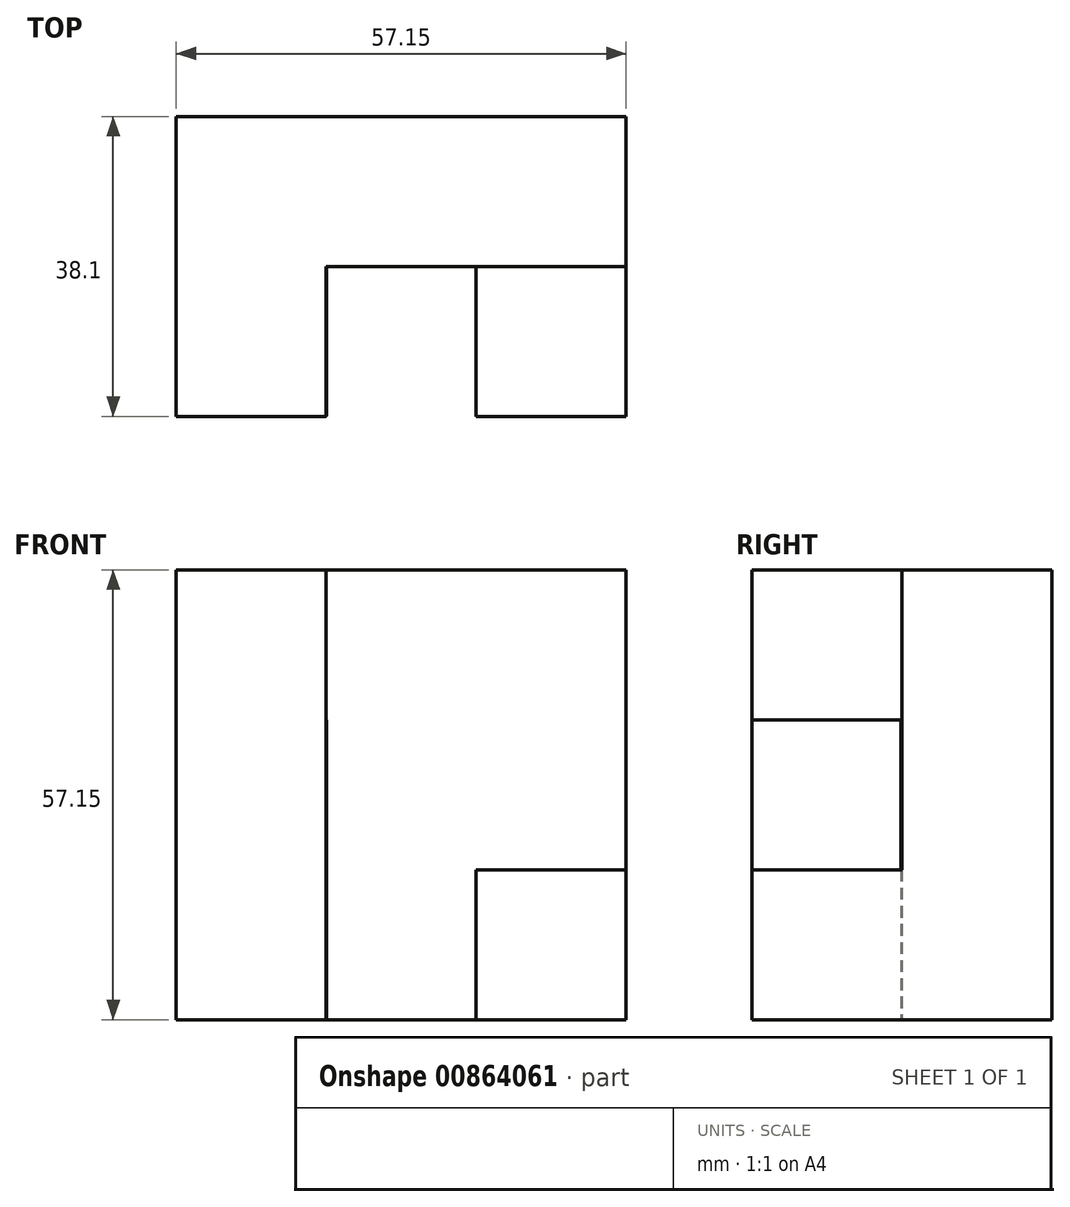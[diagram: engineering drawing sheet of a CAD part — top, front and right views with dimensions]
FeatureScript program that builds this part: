
annotation { "Feature Type Name" : "Feature", "Feature Type Description" : "" }
export const myFeature = defineFeature(function(context is Context, id is Id, definition is map)
    precondition{}
    {
        {
            var Q0;
            Q0=qCreatedBy(makeId("Front.planeOp"),FACE);
            var sketch = newSketch(context, id + "F0", { "sketchPlane" : qUnion([Q0])});
            skLineSegment(sketch, "E0", {"start": v(0, 0) * mm, "end": v(57.15, 0) * mm});
            skLineSegment(sketch, "E1", {"start": v(57.15, 0) * mm, "end": v(57.15, 19.05) * mm});
            skLineSegment(sketch, "E2", {"start": v(57.15, 19.05) * mm, "end": v(0, 19.05) * mm});
            skLineSegment(sketch, "E3", {"start": v(0, 19.05) * mm, "end": v(0, 0) * mm});
            skSolve(sketch);
        }
        {
            var Q0;
            Q0 = qSketchRegion(id + "F0", true);
            extrude(context, id + "F1", {"entities" : qUnion([Q0]), "depth" : 19.05 * mm, "offsetDistance" : 25.4 * mm});
        }
        {
            var Q0;
            Q0=makeQuery(id+"F1.opExtrude","CAP_FACE",FACE,{"disambiguationData":[OSD([sQuery(id+"F0.wireOp",EDGE,"E0"),sQuery(id+"F0.wireOp",EDGE,"E1"),sQuery(id+"F0.wireOp",EDGE,"E2"),sQuery(id+"F0.wireOp",EDGE,"E3")])],"isStart":false});
            var sketch = newSketch(context, id + "F2", { "sketchPlane" : qUnion([Q0])});
            skLineSegment(sketch, "E4.0.0", {"start": v(57.15, 19.05) * mm, "end": v(0, 19.05) * mm});
            skLineSegment(sketch, "E4.0.1", {"start": v(0, 19.05) * mm, "end": v(0, 0) * mm});
            skLineSegment(sketch, "E4.0.2", {"start": v(0, 0) * mm, "end": v(57.15, 0) * mm});
            skLineSegment(sketch, "E4.0.3", {"start": v(57.15, 0) * mm, "end": v(57.15, 19.05) * mm});
            skLineSegment(sketch, "E5", {"start": v(38.1, 19.05) * mm, "end": v(38.1, 0) * mm});
            skSolve(sketch);
        }
        {
            var Q0;
            {var subQ0=sQuery(id+"F2.wireOp",EDGE,"E4.0.3");Q0=makeQuery(id+"F2.imprint","IMPRINT",FACE,{"disambiguationData":[TD([[makeQuery(id+"F2.imprint","IMPRINT",EDGE,{"derivedFrom":subQ0}),1.0]])]});}
            extrude(context, id + "F3", {"entities" : qUnion([Q0]), "depth" : 19.05 * mm, "offsetDistance" : 25.4 * mm});
        }
        {
            var Q0;
            Q0=makeQuery(id+"F1.opExtrude","CAP_FACE",FACE,{"disambiguationData":[OSD([sQuery(id+"F0.wireOp",EDGE,"E0"),sQuery(id+"F0.wireOp",EDGE,"E1"),sQuery(id+"F0.wireOp",EDGE,"E2"),sQuery(id+"F0.wireOp",EDGE,"E3")])],"isStart":false});
            var sketch = newSketch(context, id + "F4", { "sketchPlane" : qUnion([Q0])});
            skLineSegment(sketch, "E6", {"start": v(0, 0) * mm, "end": v(19.05, 0) * mm});
            skLineSegment(sketch, "E7", {"start": v(19.05, 0) * mm, "end": v(19.05, 19.05) * mm});
            skLineSegment(sketch, "E8", {"start": v(19.05, 19.05) * mm, "end": v(0, 19.05) * mm});
            skLineSegment(sketch, "E9", {"start": v(0, 19.05) * mm, "end": v(0, 0) * mm});
            skSolve(sketch);
        }
        {
            var Q0;
            Q0=makeQuery(id+"F4.imprint","IMPRINT",FACE,{"disambiguationData":[TD([[makeQuery(id+"F4.imprint","IMPRINT",EDGE,{"derivedFrom":sQuery(id+"F4.wireOp",EDGE,"E6")}),1.0]])]});
            extrude(context, id + "F5", {"entities" : qUnion([Q0]), "operationType" : NewBodyOperationType.ADD, "depth" : 19.05 * mm, "offsetDistance" : 25.4 * mm});
        }
        {
            var Q0;
            Q0=qCreatedBy(makeId("Top.planeOp"),FACE);
            var sketch = newSketch(context, id + "F6", { "sketchPlane" : qUnion([Q0])});
            skLineSegment(sketch, "E10", {"start": v(0, -38.02) * mm, "end": v(0, -19.16) * mm});
            skLineSegment(sketch, "E11", {"start": v(0, -19.16) * mm, "end": v(19.07, -19.16) * mm});
            skLineSegment(sketch, "E12", {"start": v(19.07, -19.16) * mm, "end": v(19.07, -38.1) * mm});
            skLineSegment(sketch, "E13", {"start": v(19.07, -38.1) * mm, "end": v(0, -38.02) * mm});
            skSolve(sketch);
        }
        {
            var Q0;
            Q0 = qSketchRegion(id + "F6", true);
            var Q1;
            Q1=makeQuery(id+"F5.opExtrude","SWEPT_FACE",FACE,{"disambiguationData":[OSD([sQuery(id+"F4.wireOp",EDGE,"E8")])]});
            extrude(context, id + "F7", {"entities" : qUnion([Q0, Q1]), "operationType" : NewBodyOperationType.ADD, "depth" : 38.1 * mm, "offsetDistance" : 25.4 * mm});
        }
    });
